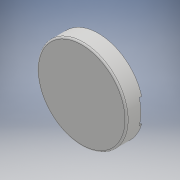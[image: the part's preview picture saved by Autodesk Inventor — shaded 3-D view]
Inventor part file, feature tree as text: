
AUTODESK INVENTOR PART (.ipt)
format: ipt  version: 2018 (Build 220112000, 112)  size: 246,272 bytes
history: native  units: mm
features: extrude x6, sketch x6, fillet x2, pattern_circular x1
ambient origin geometry x8: Origin, YZ Plane, XZ Plane, XY Plane, X Axis, Y Axis, Z Axis, Center Point
bodies: Solid1 (feature_tree)
feature tree (15):
  extrude  "Extrusion1"  Depth=0.4mm
  extrude  "Extrusion2"  Depth=10.0mm
  extrude  "Extrusion3"  Depth=27.25mm
  fillet  "Fillet1"  Radius=22.514747mm
  pattern_circular  "Circular Pattern1"  [2 undecoded]
  extrude  "Extrusion4"  Depth=1.6mm TaperAngle=0.0deg
  extrude  "Extrusion7"  Depth=0.5mm
  extrude  "Extrusion9"  Depth=1.6mm TaperAngle=360.0deg
  fillet  "Fillet5"  Radius=7.5mm
  sketch  "Sketch1"  dims[d2=0.4mm d3=0.0mm d4=54.5mm]
  sketch  "Sketch2"  dims[d5=10.0mm d6=0.0mm d7=56.0mm]
  sketch  "Sketch3"  dims[d8=56.0mm d9=27.25mm d10=22.514747mm]
  sketch  "Sketch4"  dims[d11=0.698132mm]
  sketch  "Sketch7"  dims[d12=26.25mm]
  sketch  "Sketch9"  dims[d13=22.514747mm d14=0.698132mm d15=1.2mm d16=0.0mm d17=0.5mm d18=20.0mm d19=360.0deg d25=7.5mm d26=3.0mm d27=7.5mm d28=3.0mm d29=1.5mm d30=0.0mm d47=48.0mm d48=6.5mm d49=0.0mm d50=54.5mm d51=3.0mm d52=7.5mm d53=3.0mm d54=7.5mm d55=1.0mm d56=0.5mm d60=36.0mm d61=1.6mm d62=0.0mm]
note: 2 required parameter values undecoded (feature->parameter linkage not recoverable at this tier; creation-order binding heuristic only, values carry confidence <= 0.55)
